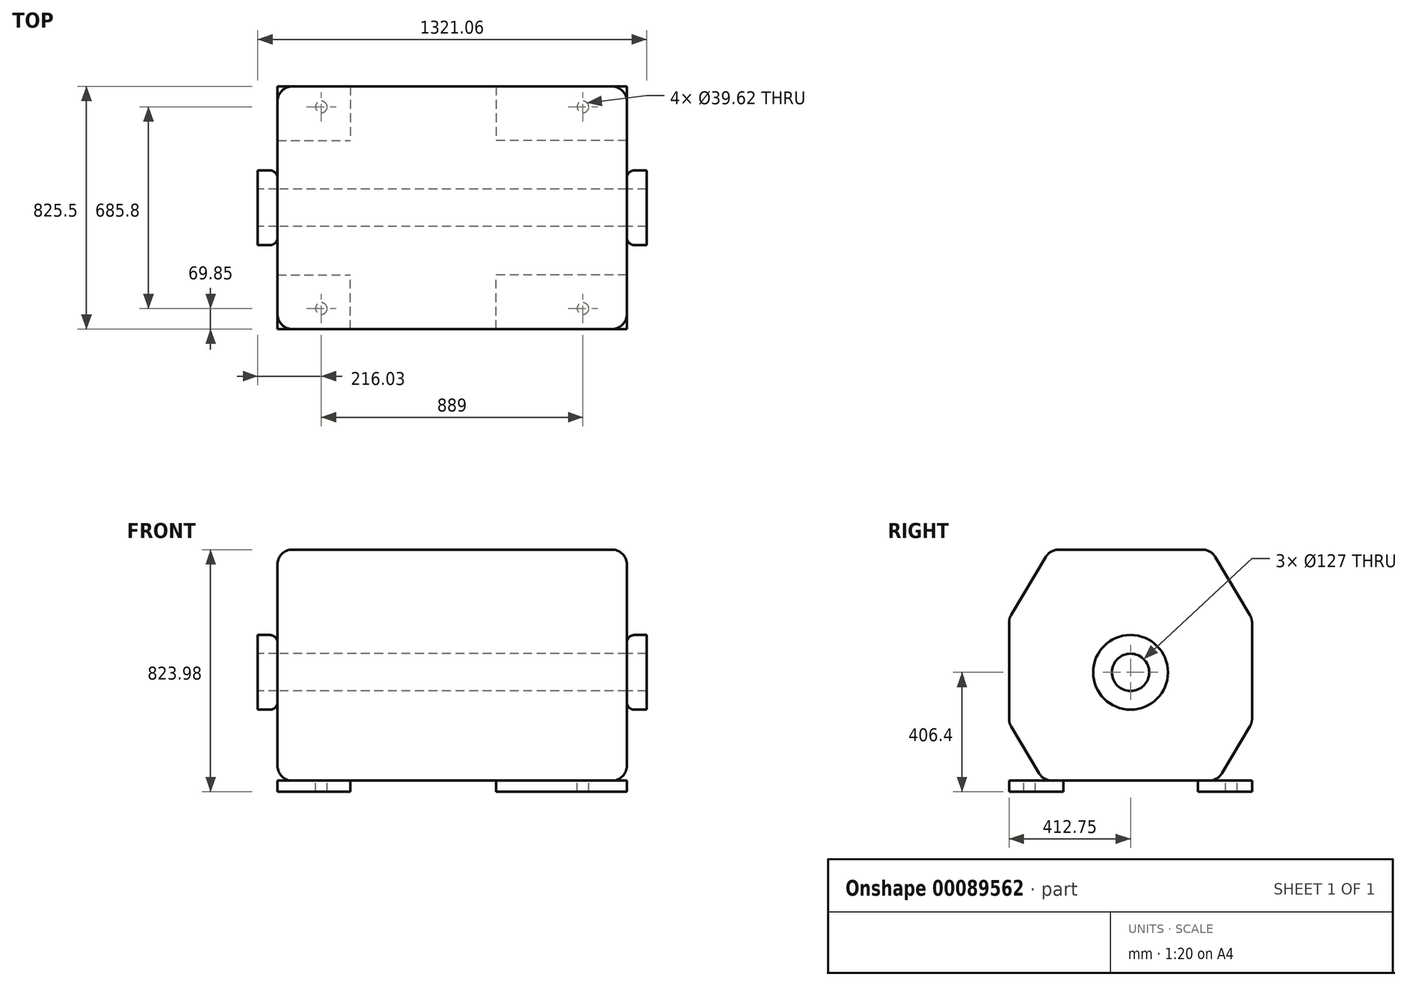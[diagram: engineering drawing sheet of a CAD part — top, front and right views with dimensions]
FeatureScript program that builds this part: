
annotation { "Feature Type Name" : "Feature", "Feature Type Description" : "" }
export const myFeature = defineFeature(function(context is Context, id is Id, definition is map)
    precondition{}
    {
        {
            var Q0;
            Q0=qCreatedBy(makeId("Top.planeOp"),FACE);
            var sketch = newSketch(context, id + "F0", { "sketchPlane" : qUnion([Q0])});
            skLineSegment(sketch, "E0.rect.bottom", {"start": v(-593.73, 412.75) * mm, "end": v(593.73, 412.75) * mm, "construction": true});
            skLineSegment(sketch, "E0.rect.top", {"start": v(-593.73, -412.75) * mm, "end": v(593.73, -412.75) * mm, "construction": true});
            skLineSegment(sketch, "E0.rect.left", {"start": v(-593.72, 412.75) * mm, "end": v(-593.73, -412.75) * mm, "construction": true});
            skLineSegment(sketch, "E0.rect.right", {"start": v(593.73, 412.75) * mm, "end": v(593.73, -412.75) * mm, "construction": true});
            skPoint(sketch, "E0.rect.middle", {"position": v(0, 0) * mm});
            skLineSegment(sketch, "E1", {"start": v(0, 412.75) * mm, "end": v(0, -412.75) * mm, "construction": true});
            skLineSegment(sketch, "E2", {"start": v(-593.73, 0) * mm, "end": v(593.73, 0) * mm, "construction": true});
            skLineSegment(sketch, "E3.bottom", {"start": v(-593.73, 412.75) * mm, "end": v(-346.08, 412.75) * mm});
            skLineSegment(sketch, "E3.top", {"start": v(-593.73, 228.6) * mm, "end": v(-346.08, 228.6) * mm});
            skLineSegment(sketch, "E3.left", {"start": v(-593.73, 412.75) * mm, "end": v(-593.73, 228.6) * mm});
            skLineSegment(sketch, "E3.right", {"start": v(-346.08, 412.75) * mm, "end": v(-346.08, 228.6) * mm});
            skLineSegment(sketch, "E4.bottom", {"start": v(593.73, 412.75) * mm, "end": v(149.23, 412.75) * mm});
            skLineSegment(sketch, "E4.top", {"start": v(593.73, 228.6) * mm, "end": v(149.23, 228.6) * mm});
            skLineSegment(sketch, "E4.left", {"start": v(593.73, 412.75) * mm, "end": v(593.73, 228.6) * mm});
            skLineSegment(sketch, "E4.right", {"start": v(149.23, 412.75) * mm, "end": v(149.23, 228.6) * mm});
            skLineSegment(sketch, "E5.0", {"start": v(-593.73, 342.9) * mm, "end": v(593.73, 342.9) * mm, "construction": true});
            skLineSegment(sketch, "E6.0", {"start": v(-444.5, 412.75) * mm, "end": v(-444.5, -412.75) * mm, "construction": true});
            skCircle(sketch, "E7", {"center": v(-444.5, 342.9) * mm, "radius": 19.81 * mm});
            skCircle(sketch, "E8.MirrorC", {"center": v(444.5, 342.9) * mm, "radius": 19.81 * mm});
            skCircle(sketch, "E9.MirrorC", {"center": v(-444.5, -342.9) * mm, "radius": 19.81 * mm});
            skLineSegment(sketch, "E10.MirrorCS", {"start": v(-593.73, -228.6) * mm, "end": v(-346.08, -228.6) * mm});
            skLineSegment(sketch, "E11.MirrorCS", {"start": v(-593.73, -412.75) * mm, "end": v(-593.73, -228.6) * mm});
            skLineSegment(sketch, "E12.MirrorCS", {"start": v(-346.08, -412.75) * mm, "end": v(-346.08, -228.6) * mm});
            skLineSegment(sketch, "E13.MirrorCS", {"start": v(149.23, -412.75) * mm, "end": v(149.23, -228.6) * mm});
            skCircle(sketch, "E14.MirrorC", {"center": v(444.5, -342.9) * mm, "radius": 19.81 * mm});
            skLineSegment(sketch, "E15.MirrorCS", {"start": v(-593.73, -412.75) * mm, "end": v(593.73, -412.75) * mm});
            skLineSegment(sketch, "E16.MirrorCS", {"start": v(593.73, -228.6) * mm, "end": v(149.23, -228.6) * mm});
            skLineSegment(sketch, "E17.MirrorCS", {"start": v(-593.73, -342.9) * mm, "end": v(593.73, -342.9) * mm, "construction": true});
            skLineSegment(sketch, "E18.MirrorCS", {"start": v(593.73, -412.75) * mm, "end": v(149.23, -412.75) * mm});
            skLineSegment(sketch, "E19.MirrorCS", {"start": v(-593.73, -412.75) * mm, "end": v(-346.08, -412.75) * mm});
            skLineSegment(sketch, "E20.MirrorCS", {"start": v(593.73, -412.75) * mm, "end": v(593.73, -228.6) * mm});
            skSolve(sketch);
        }
        {
            var Q0;
            Q0=qSketchRegion(id+"F0",true);
            extrude(context, id + "F1", {"entities" : qUnion([Q0]), "oppositeDirection" : true, "depth" : 38.1 * mm});
        }
        {
            var Q0;
            Q0=qCreatedBy(makeId("Right.planeOp"),FACE);
            var sketch = newSketch(context, id + "F2", { "sketchPlane" : qUnion([Q0])});
            skLineSegment(sketch, "E21.0", {"start": v(-228.6, -38.1) * mm, "end": v(-228.6, 0) * mm, "construction": true});
            skLineSegment(sketch, "E22.0", {"start": v(228.6, -38.1) * mm, "end": v(228.6, 0) * mm, "construction": true});
            skLineSegment(sketch, "E23", {"start": v(-228.6, -38.1) * mm, "end": v(228.6, -38.1) * mm, "construction": true});
            skLineSegment(sketch, "E24.0", {"start": v(-228.6, 785.88) * mm, "end": v(412.75, 785.88) * mm, "construction": true});
            skLineSegment(sketch, "E25.0.0", {"start": v(-228.6, 0) * mm, "end": v(-412.75, 0) * mm, "construction": true});
            skLineSegment(sketch, "E25.0.1", {"start": v(-412.75, 0) * mm, "end": v(-412.75, -38.1) * mm, "construction": true});
            skLineSegment(sketch, "E25.0.2", {"start": v(-412.75, -38.1) * mm, "end": v(-228.6, -38.1) * mm, "construction": true});
            skLineSegment(sketch, "E26.0.0", {"start": v(412.75, 0) * mm, "end": v(228.6, 0) * mm, "construction": true});
            skLineSegment(sketch, "E26.0.1", {"start": v(228.6, 0) * mm, "end": v(228.6, -38.1) * mm, "construction": true});
            skLineSegment(sketch, "E26.0.2", {"start": v(228.6, -38.1) * mm, "end": v(412.75, -38.1) * mm, "construction": true});
            skLineSegment(sketch, "E26.0.3", {"start": v(412.75, -38.1) * mm, "end": v(412.75, 785.88) * mm, "construction": true});
            skLineSegment(sketch, "E27.bottom", {"start": v(273.05, 785.88) * mm, "end": v(-273.05, 785.88) * mm});
            skLineSegment(sketch, "E27.top", {"start": v(412.75, 0) * mm, "end": v(-412.75, 0) * mm});
            skLineSegment(sketch, "E27.left", {"start": v(412.75, 785.88) * mm, "end": v(412.75, 196.09) * mm});
            skLineSegment(sketch, "E27.right", {"start": v(-412.75, 551.69) * mm, "end": v(-412.75, 196.09) * mm});
            skLineSegment(sketch, "E28.0", {"start": v(-273.05, 785.88) * mm, "end": v(-273.05, 0) * mm, "construction": true});
            skLineSegment(sketch, "E29", {"start": v(412.75, 373.89) * mm, "end": v(-412.75, 373.89) * mm, "construction": true});
            skLineSegment(sketch, "E30.0", {"start": v(412.75, 551.69) * mm, "end": v(-412.75, 551.69) * mm, "construction": true});
            skLineSegment(sketch, "E31", {"start": v(-412.75, 551.69) * mm, "end": v(-273.05, 785.88) * mm});
            skLineSegment(sketch, "E32.MirrorCS", {"start": v(-412.75, 196.09) * mm, "end": v(-273.05, -38.1) * mm});
            skLineSegment(sketch, "E33", {"start": v(0, 785.88) * mm, "end": v(0, -289.7) * mm, "construction": true});
            skLineSegment(sketch, "E34.MirrorCS", {"start": v(412.75, 551.69) * mm, "end": v(273.05, 785.88) * mm});
            skLineSegment(sketch, "E35.MirrorCS", {"start": v(412.75, 196.09) * mm, "end": v(273.05, -38.1) * mm});
            skPoint(sketch, "E36.orphan", {"position": v(-412.75, 785.88) * mm});
            skSolve(sketch);
        }
        {
            var Q0;
            Q0=qSketchRegion(id+"F2",true);
            var Q1;
            Q1=makeQuery(id+"F1.opExtrude","SWEPT_FACE",FACE,{"disambiguationData":[OSD([sQuery(id+"F0.wireOp",EDGE,"E20.MirrorCS")])]});
            var Q2;
            Q2=makeQuery(id+"F1.opExtrude","SWEPT_FACE",FACE,{"disambiguationData":[OSD([sQuery(id+"F0.wireOp",EDGE,"E3.left")])]});
            extrude(context, id + "F3", {"entities" : qUnion([Q0]), "endBound" : BoundingType.UP_TO_SURFACE, "endBoundEntityFace" : qUnion([Q1]), "depth" : 25.4 * mm, "hasSecondDirection" : true, "secondDirectionBound" : SecondDirectionBoundingType.UP_TO_SURFACE, "secondDirectionOppositeDirection" : true, "secondDirectionBoundEntityFace" : qUnion([Q2]), "secondDirectionDepth" : 25.4 * mm});
        }
        {
            var Q0;
            Q0=makeQuery(id+"F3.opExtrude","CAP_FACE",FACE,{"disambiguationData":[OSD([sQuery(id+"F2.wireOp",EDGE,"E27.bottom"),sQuery(id+"F2.wireOp",EDGE,"E27.top"),sQuery(id+"F2.wireOp",EDGE,"E27.left"),sQuery(id+"F2.wireOp",EDGE,"E27.right"),sQuery(id+"F2.wireOp",EDGE,"E31"),sQuery(id+"F2.wireOp",EDGE,"E32.MirrorCS"),sQuery(id+"F2.wireOp",EDGE,"E34.MirrorCS"),sQuery(id+"F2.wireOp",EDGE,"E35.MirrorCS")])],"isStart":false});
            var Q1;
            Q1=makeQuery(id+"F3.opExtrude","CAP_FACE",FACE,{"disambiguationData":[OSD([sQuery(id+"F2.wireOp",EDGE,"E27.bottom"),sQuery(id+"F2.wireOp",EDGE,"E27.top"),sQuery(id+"F2.wireOp",EDGE,"E27.left"),sQuery(id+"F2.wireOp",EDGE,"E27.right"),sQuery(id+"F2.wireOp",EDGE,"E31"),sQuery(id+"F2.wireOp",EDGE,"E32.MirrorCS"),sQuery(id+"F2.wireOp",EDGE,"E34.MirrorCS"),sQuery(id+"F2.wireOp",EDGE,"E35.MirrorCS")])],"isStart":true});
            var Q2;
            Q2=makeQuery(id+"F3.opExtrude","SWEPT_FACE",FACE,{"disambiguationData":[OSD([sQuery(id+"F2.wireOp",EDGE,"E35.MirrorCS")])]});
            var Q3;
            Q3=makeQuery(id+"F3.opExtrude","SWEPT_FACE",FACE,{"disambiguationData":[OSD([sQuery(id+"F2.wireOp",EDGE,"E27.left")])]});
            var Q4;
            Q4=makeQuery(id+"F3.opExtrude","SWEPT_FACE",FACE,{"disambiguationData":[OSD([sQuery(id+"F2.wireOp",EDGE,"E34.MirrorCS")])]});
            var Q5;
            Q5=makeQuery(id+"F3.opExtrude","SWEPT_FACE",FACE,{"disambiguationData":[OSD([sQuery(id+"F2.wireOp",EDGE,"E31")])]});
            var Q6;
            Q6=makeQuery(id+"F3.opExtrude","SWEPT_FACE",FACE,{"disambiguationData":[OSD([sQuery(id+"F2.wireOp",EDGE,"E27.right")])]});
            var Q7;
            Q7=makeQuery(id+"F3.opExtrude","SWEPT_FACE",FACE,{"disambiguationData":[OSD([sQuery(id+"F2.wireOp",EDGE,"E32.MirrorCS")])]});
            fillet(context, id + "F4", {"entities" : qUnion([Q0, Q1, Q2, Q3, Q4, Q5, Q6, Q7]), "radius" : 50.8 * mm, "tangentPropagation" : true, "allowEdgeOverflow" : false});
        }
        {
            var Q0;
            Q0=makeQuery(id+"F3.opExtrude","CAP_FACE",FACE,{"disambiguationData":[OSD([sQuery(id+"F2.wireOp",EDGE,"E27.bottom"),sQuery(id+"F2.wireOp",EDGE,"E27.top"),sQuery(id+"F2.wireOp",EDGE,"E27.left"),sQuery(id+"F2.wireOp",EDGE,"E27.right"),sQuery(id+"F2.wireOp",EDGE,"E31"),sQuery(id+"F2.wireOp",EDGE,"E32.MirrorCS"),sQuery(id+"F2.wireOp",EDGE,"E34.MirrorCS"),sQuery(id+"F2.wireOp",EDGE,"E35.MirrorCS")])],"isStart":true});
            var sketch = newSketch(context, id + "F5", { "sketchPlane" : qUnion([Q0])});
            skLineSegment(sketch, "E37", {"start": v(0, 0) * mm, "end": v(0, 911.74) * mm, "construction": true});
            skLineSegment(sketch, "E38.0", {"start": v(-412.75, -38.1) * mm, "end": v(-228.6, -38.1) * mm, "construction": true});
            skLineSegment(sketch, "E39", {"start": v(-228.6, -38.1) * mm, "end": v(229.54, -38.1) * mm, "construction": true});
            skLineSegment(sketch, "E40.0", {"start": v(-228.6, 368.3) * mm, "end": v(229.54, 368.3) * mm, "construction": true});
            skCircle(sketch, "E41", {"center": v(0, 368.3) * mm, "radius": 127 * mm});
            skSolve(sketch);
        }
        {
            var Q0;
            Q0=qSketchRegion(id+"F5",true);
            extrude(context, id + "F6", {"entities" : qUnion([Q0]), "depth" : 66.8 * mm});
        }
        {
            var Q0;
            Q0=makeQuery(id+"F6.opExtrude","SWEPT_BODY",BODY,{"disambiguationData":[OSD([sQuery(id+"F5.wireOp",EDGE,"E41")])]});
            var Q1;
            Q1=qCreatedBy(makeId("Right.planeOp"),FACE);
            mirror(context, id + "F7", {"entities" : qUnion([Q0]), "mirrorPlane" : qUnion([Q1])});
        }
        {
            var Q0;
            Q0=makeQuery(id+"F7.opPattern","COPY",EDGE,{"derivedFrom":makeQuery(id+"F6.opExtrude","CAP_EDGE",EDGE,{"disambiguationData":[OSD([sQuery(id+"F5.wireOp",EDGE,"E41")])],"isStart":true}),"instanceName":"1"});
            var Q1;
            Q1=makeQuery(id+"F6.opExtrude","CAP_EDGE",EDGE,{"disambiguationData":[OSD([sQuery(id+"F5.wireOp",EDGE,"E41")])],"isStart":true});
            fillet(context, id + "F8", {"entities" : qUnion([Q0, Q1]), "radius" : 25.4 * mm, "tangentPropagation" : true, "allowEdgeOverflow" : false});
        }
        {
            var Q0;
            Q0=makeQuery(id+"F6.opExtrude","CAP_FACE",FACE,{"disambiguationData":[OSD([sQuery(id+"F5.wireOp",EDGE,"E41")])],"isStart":false});
            var sketch = newSketch(context, id + "F9", { "sketchPlane" : qUnion([Q0])});
            skCircle(sketch, "E42", {"center": v(0, 368.3) * mm, "radius": 63.5 * mm});
            skSolve(sketch);
        }
        {
            var Q0;
            Q0=qSketchRegion(id+"F9",true);
            extrude(context, id + "F10", {"entities" : qUnion([Q0]), "operationType" : NewBodyOperationType.REMOVE, "endBound" : BoundingType.THROUGH_ALL, "oppositeDirection" : true, "depth" : 25.4 * mm});
        }
    });
